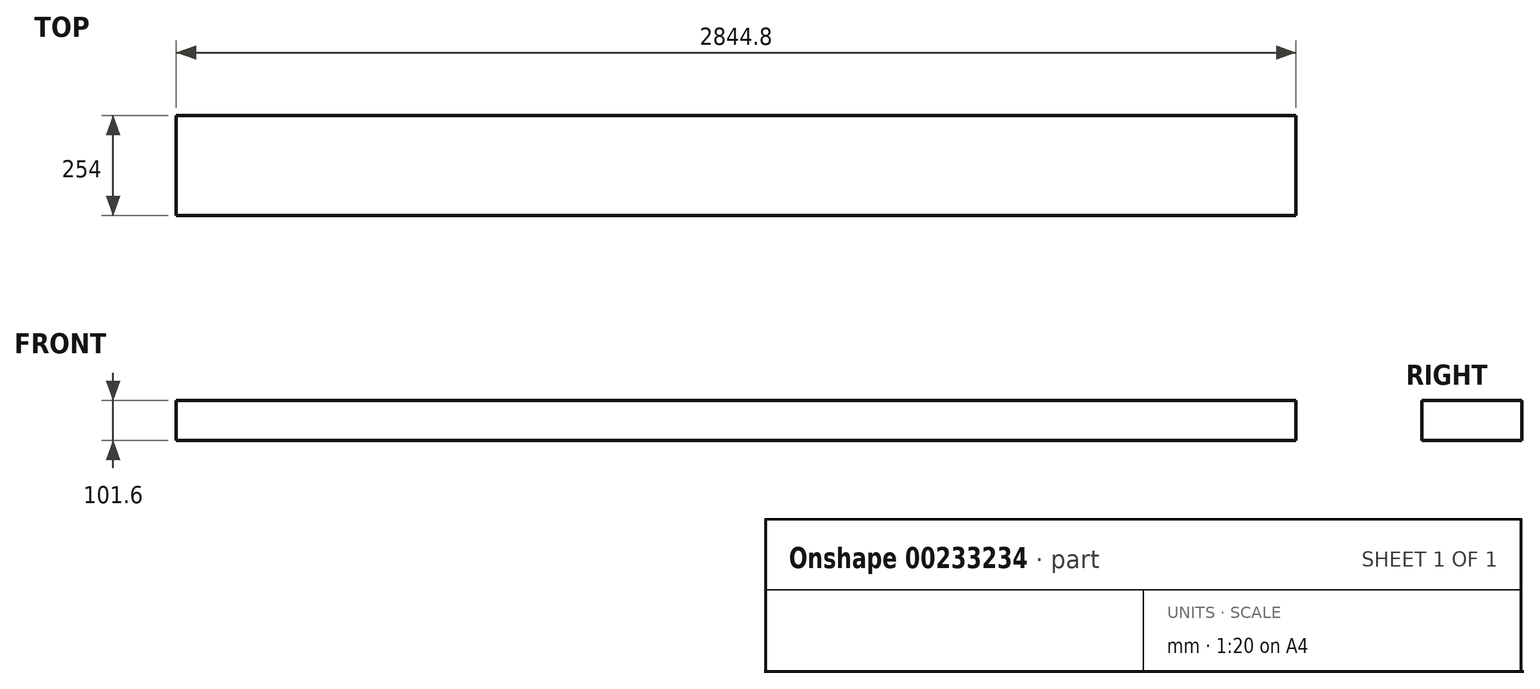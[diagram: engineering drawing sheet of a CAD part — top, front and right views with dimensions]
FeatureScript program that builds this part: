
annotation { "Feature Type Name" : "Feature", "Feature Type Description" : "" }
export const myFeature = defineFeature(function(context is Context, id is Id, definition is map)
    precondition{}
    {
        {
            var Q0;
            Q0=qCreatedBy(makeId("Top.planeOp"),FACE);
            var sketch = newSketch(context, id + "F0", { "sketchPlane" : qUnion([Q0])});
            skLineSegment(sketch, "E0.bottom", {"start": v(-664.24, 160.42) * mm, "end": v(2180.56, 160.42) * mm});
            skLineSegment(sketch, "E0.top", {"start": v(-664.24, -93.58) * mm, "end": v(2180.56, -93.58) * mm});
            skLineSegment(sketch, "E0.left", {"start": v(-664.24, 160.42) * mm, "end": v(-664.24, -93.58) * mm});
            skLineSegment(sketch, "E0.right", {"start": v(2180.56, 160.42) * mm, "end": v(2180.56, -93.58) * mm});
            skSolve(sketch);
        }
        {
            var Q0;
            Q0 = qSketchRegion(id + "F0", true);
            extrude(context, id + "F1", {"entities" : qUnion([Q0]), "depth" : 101.6 * mm});
        }
    });
